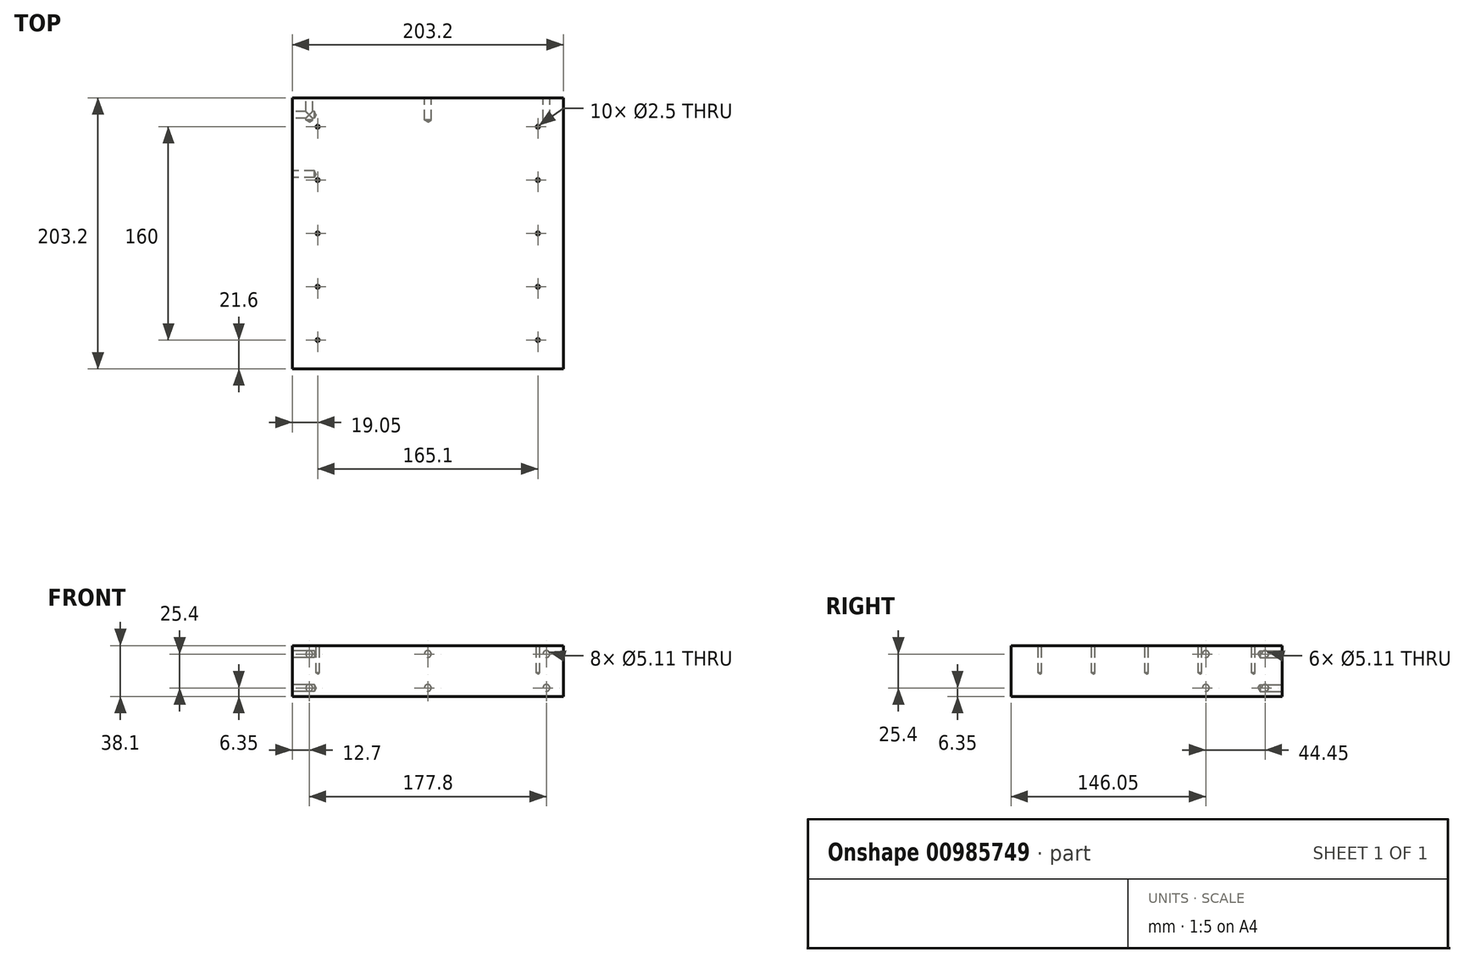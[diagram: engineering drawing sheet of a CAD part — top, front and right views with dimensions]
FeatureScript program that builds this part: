
annotation { "Feature Type Name" : "Feature", "Feature Type Description" : "" }
export const myFeature = defineFeature(function(context is Context, id is Id, definition is map)
    precondition{}
    {
        {
            var Q0;
            Q0=qCreatedBy(makeId("Top.planeOp"),FACE);
            var sketch = newSketch(context, id + "F0", { "sketchPlane" : qUnion([Q0])});
            skLineSegment(sketch, "E0.bottom", {"start": v(-101.6, 0) * mm, "end": v(101.6, 0) * mm});
            skLineSegment(sketch, "E0.top", {"start": v(-101.6, 203.2) * mm, "end": v(101.6, 203.2) * mm});
            skLineSegment(sketch, "E0.left", {"start": v(-101.6, 0) * mm, "end": v(-101.6, 203.2) * mm});
            skLineSegment(sketch, "E0.right", {"start": v(101.6, 0) * mm, "end": v(101.6, 203.2) * mm});
            skSolve(sketch);
        }
        {
            var Q0;
            Q0 = qSketchRegion(id + "F0", true);
            extrude(context, id + "F1", {"entities" : qUnion([Q0]), "depth" : 38.1 * mm, "offsetDistance" : 25.4 * mm});
        }
        {
            var Q0;
            {var subQ0=sQuery(id+"F0.wireOp",EDGE,"E0.bottom");var subQ2=sQuery(id+"F0.wireOp",EDGE,"E0.left");Q0=makeQuery(id+"FGkV8nF4XjDxECF_1.boolean.opBoolean","SPLIT",FACE,{"disambiguationData":[TD([makeQuery(id+"F1.opExtrude","SWEPT_FACE",FACE,{"disambiguationData":[OSD([subQ0])]})])],"derivedFrom":makeQuery(id+"F1.opExtrude","SWEPT_FACE",FACE,{"disambiguationData":[OSD([subQ2])]})});}
            var sketch = newSketch(context, id + "F2", { "sketchPlane" : qUnion([Q0])});
            skLineSegment(sketch, "E1", {"start": v(-190.5, 31.75) * mm, "end": v(-190.5, 6.35) * mm, "construction": true});
            skLineSegment(sketch, "E2", {"start": v(-190.5, 6.35) * mm, "end": v(-146.05, 6.35) * mm, "construction": true});
            skLineSegment(sketch, "E3", {"start": v(-146.05, 6.35) * mm, "end": v(-146.05, 31.75) * mm, "construction": true});
            skLineSegment(sketch, "E4", {"start": v(-146.05, 31.75) * mm, "end": v(-190.5, 31.75) * mm, "construction": true});
            skLineSegment(sketch, "E5", {"start": v(-203.2, 19.05) * mm, "end": v(-190.5, 19.05) * mm, "construction": true});
            skPoint(sketch, "E6", {"position": v(-190.5, 31.75) * mm});
            skPoint(sketch, "E7", {"position": v(-190.5, 6.35) * mm});
            skPoint(sketch, "E8", {"position": v(-146.05, 6.35) * mm});
            skPoint(sketch, "E9", {"position": v(-146.05, 31.75) * mm});
            skSolve(sketch);
        }
        {
            var Q0;
            Q0=sQuery(id+"F2.wireOp",VERTEX,"E6");
            var Q1;
            Q1=sQuery(id+"F2.wireOp",VERTEX,"E7");
            var Q2;
            Q2=sQuery(id+"F2.wireOp",VERTEX,"E8");
            var Q3;
            Q3=sQuery(id+"F2.wireOp",VERTEX,"E9");
            var Q4;
            Q4=makeQuery(id+"F1.opExtrude","SWEPT_BODY",BODY,{"disambiguationData":[OSD([sQuery(id+"F0.wireOp",EDGE,"E0.bottom"),sQuery(id+"F0.wireOp",EDGE,"E0.top"),sQuery(id+"F0.wireOp",EDGE,"E0.left"),sQuery(id+"F0.wireOp",EDGE,"E0.right")])]});
            hole(context, id + "F3", {"style" : HoleStyle.SIMPLE, "endStyle" : HoleEndStyle.BLIND, "standardTappedOrClearance" : lookupTablePath({ "standard" : "ANSI", "engagement" : "75%", "pitch" : "20 tpi", "size" : "1/4", "type" : "Tapped" }), "standardBlindInLast" : lookupTablePath({ "standard" : "ANSI", "fit" : "Free", "engagement" : "75%", "pitch" : "20 tpi", "size" : "1/4", "type" : "Clearance & tapped" }), "holeDiameter" : 5.1 * mm, "majorDiameter" : 6.35 * mm, "showTappedDepth" : true, "holeDepth" : 16.51 * mm, "isTappedThrough" : true, "tappedDepth" : 12.7 * mm, "tapClearance" : 3, "startFromSketch" : true, "locations" : qUnion([Q0, Q1, Q2, Q3]), "scope" : qUnion([Q4])});
        }
        {
            var Q0;
            Q0=makeQuery(id+"F1.opExtrude","SWEPT_FACE",FACE,{"disambiguationData":[OSD([sQuery(id+"F0.wireOp",EDGE,"E0.top")])]});
            var sketch = newSketch(context, id + "F4", { "sketchPlane" : qUnion([Q0])});
            skLineSegment(sketch, "E10", {"start": v(-88.9, 6.35) * mm, "end": v(-88.9, 31.75) * mm, "construction": true});
            skLineSegment(sketch, "E11", {"start": v(-88.9, 31.75) * mm, "end": v(88.9, 31.75) * mm, "construction": true});
            skLineSegment(sketch, "E12", {"start": v(88.9, 31.75) * mm, "end": v(88.9, 6.35) * mm, "construction": true});
            skLineSegment(sketch, "E13", {"start": v(88.9, 6.35) * mm, "end": v(-88.9, 6.35) * mm, "construction": true});
            skLineSegment(sketch, "E14", {"start": v(0, 31.75) * mm, "end": v(0, 38.1) * mm, "construction": true});
            skLineSegment(sketch, "E15", {"start": v(-88.9, 19.05) * mm, "end": v(-101.6, 19.05) * mm, "construction": true});
            skPoint(sketch, "E16", {"position": v(-88.9, 31.75) * mm});
            skPoint(sketch, "E17", {"position": v(88.9, 31.75) * mm});
            skPoint(sketch, "E18", {"position": v(88.9, 6.35) * mm});
            skPoint(sketch, "E19", {"position": v(-88.9, 6.35) * mm});
            skPoint(sketch, "E20", {"position": v(0, 31.75) * mm});
            skPoint(sketch, "E21", {"position": v(0, 6.35) * mm});
            skSolve(sketch);
        }
        {
            var Q0;
            Q0=sQuery(id+"F4.wireOp",VERTEX,"E16");
            var Q1;
            Q1=sQuery(id+"F4.wireOp",VERTEX,"E19");
            var Q2;
            Q2=sQuery(id+"F4.wireOp",VERTEX,"E17");
            var Q3;
            Q3=sQuery(id+"F4.wireOp",VERTEX,"E18");
            var Q4;
            Q4=sQuery(id+"F4.wireOp",VERTEX,"E20");
            var Q5;
            Q5=sQuery(id+"F4.wireOp",VERTEX,"E21");
            var Q6;
            Q6=makeQuery(id+"F1.opExtrude","SWEPT_BODY",BODY,{"disambiguationData":[OSD([sQuery(id+"F0.wireOp",EDGE,"E0.bottom"),sQuery(id+"F0.wireOp",EDGE,"E0.top"),sQuery(id+"F0.wireOp",EDGE,"E0.left"),sQuery(id+"F0.wireOp",EDGE,"E0.right")])]});
            hole(context, id + "F5", {"style" : HoleStyle.SIMPLE, "endStyle" : HoleEndStyle.BLIND, "standardTappedOrClearance" : lookupTablePath({ "standard" : "ANSI", "engagement" : "75%", "pitch" : "20 tpi", "size" : "1/4", "type" : "Tapped" }), "standardBlindInLast" : lookupTablePath({ "standard" : "ANSI", "fit" : "Free", "engagement" : "75%", "pitch" : "20 tpi", "size" : "1/4", "type" : "Clearance & tapped" }), "holeDiameter" : 5.1 * mm, "majorDiameter" : 6.35 * mm, "showTappedDepth" : true, "holeDepth" : 16.51 * mm, "isTappedThrough" : true, "tappedDepth" : 12.7 * mm, "tapClearance" : 3, "startFromSketch" : true, "locations" : qUnion([Q0, Q1, Q2, Q3, Q4, Q5]), "scope" : qUnion([Q6])});
        }
        {
            var Q0;
            Q0=makeQuery(id+"F1.opExtrude","CAP_FACE",FACE,{"disambiguationData":[OSD([sQuery(id+"F0.wireOp",EDGE,"E0.bottom"),sQuery(id+"F0.wireOp",EDGE,"E0.top"),sQuery(id+"F0.wireOp",EDGE,"E0.left"),sQuery(id+"F0.wireOp",EDGE,"E0.right")])],"isStart":false});
            var sketch = newSketch(context, id + "F6", { "sketchPlane" : qUnion([Q0])});
            skLineSegment(sketch, "E22", {"start": v(-82.55, 21.6) * mm, "end": v(-82.55, 61.6) * mm, "construction": true});
            skLineSegment(sketch, "E23", {"start": v(-82.55, 61.6) * mm, "end": v(-82.55, 101.6) * mm, "construction": true});
            skLineSegment(sketch, "E24", {"start": v(-82.55, 101.6) * mm, "end": v(-82.55, 141.6) * mm, "construction": true});
            skLineSegment(sketch, "E25", {"start": v(-82.55, 141.6) * mm, "end": v(-82.55, 181.6) * mm, "construction": true});
            skLineSegment(sketch, "E26", {"start": v(-82.55, 181.6) * mm, "end": v(82.55, 181.6) * mm, "construction": true});
            skLineSegment(sketch, "E27", {"start": v(82.55, 181.6) * mm, "end": v(82.55, 141.6) * mm, "construction": true});
            skLineSegment(sketch, "E28", {"start": v(82.55, 141.6) * mm, "end": v(-82.55, 141.6) * mm, "construction": true});
            skLineSegment(sketch, "E29", {"start": v(-82.55, 101.6) * mm, "end": v(82.55, 101.6) * mm, "construction": true});
            skLineSegment(sketch, "E30", {"start": v(82.55, 141.6) * mm, "end": v(82.55, 101.6) * mm, "construction": true});
            skLineSegment(sketch, "E31", {"start": v(82.55, 101.6) * mm, "end": v(82.55, 61.6) * mm, "construction": true});
            skLineSegment(sketch, "E32", {"start": v(82.55, 61.6) * mm, "end": v(82.55, 21.6) * mm, "construction": true});
            skLineSegment(sketch, "E33", {"start": v(82.55, 21.6) * mm, "end": v(-82.55, 21.6) * mm, "construction": true});
            skLineSegment(sketch, "E34", {"start": v(-82.55, 61.6) * mm, "end": v(82.55, 61.6) * mm, "construction": true});
            skLineSegment(sketch, "E35", {"start": v(0, 21.6) * mm, "end": v(0, 0) * mm, "construction": true});
            skLineSegment(sketch, "E36", {"start": v(0, 181.6) * mm, "end": v(0, 203.2) * mm, "construction": true});
            skPoint(sketch, "E37", {"position": v(-82.55, 181.6) * mm});
            skPoint(sketch, "E38", {"position": v(-82.55, 141.6) * mm});
            skPoint(sketch, "E39", {"position": v(-82.55, 101.6) * mm});
            skPoint(sketch, "E40", {"position": v(-82.55, 61.6) * mm});
            skPoint(sketch, "E41", {"position": v(-82.55, 21.6) * mm});
            skPoint(sketch, "E42", {"position": v(82.55, 21.6) * mm});
            skPoint(sketch, "E43", {"position": v(82.55, 61.6) * mm});
            skPoint(sketch, "E44", {"position": v(82.55, 101.6) * mm});
            skPoint(sketch, "E45", {"position": v(82.55, 141.6) * mm});
            skPoint(sketch, "E46", {"position": v(82.55, 181.6) * mm});
            skSolve(sketch);
        }
        {
            var Q0;
            Q0=sQuery(id+"F6.wireOp",VERTEX,"E37");
            var Q1;
            Q1=sQuery(id+"F6.wireOp",VERTEX,"E38");
            var Q2;
            Q2=sQuery(id+"F6.wireOp",VERTEX,"E39");
            var Q3;
            Q3=sQuery(id+"F6.wireOp",VERTEX,"E40");
            var Q4;
            Q4=sQuery(id+"F6.wireOp",VERTEX,"E41");
            var Q5;
            Q5=sQuery(id+"F6.wireOp",VERTEX,"E42");
            var Q6;
            Q6=sQuery(id+"F6.wireOp",VERTEX,"E43");
            var Q7;
            Q7=sQuery(id+"F6.wireOp",VERTEX,"E44");
            var Q8;
            Q8=sQuery(id+"F6.wireOp",VERTEX,"E45");
            var Q9;
            Q9=sQuery(id+"F6.wireOp",VERTEX,"E46");
            var Q10;
            Q10=makeQuery(id+"F1.opExtrude","SWEPT_BODY",BODY,{"disambiguationData":[OSD([sQuery(id+"F0.wireOp",EDGE,"E0.bottom"),sQuery(id+"F0.wireOp",EDGE,"E0.top"),sQuery(id+"F0.wireOp",EDGE,"E0.left"),sQuery(id+"F0.wireOp",EDGE,"E0.right")])]});
            hole(context, id + "F7", {"style" : HoleStyle.SIMPLE, "endStyle" : HoleEndStyle.BLIND, "standardTappedOrClearance" : lookupTablePath({ "standard" : "ISO", "engagement" : "75%", "pitch" : "0.5 mm", "size" : "M3", "type" : "Tapped" }), "standardBlindInLast" : lookupTablePath({ "standard" : "ISO", "fit" : "Normal", "engagement" : "75%", "pitch" : "0.5 mm", "size" : "M3", "type" : "Clearance & tapped" }), "holeDiameter" : 2.5 * mm, "majorDiameter" : 3 * mm, "showTappedDepth" : true, "holeDepth" : 20.55 * mm, "isTappedThrough" : true, "tappedDepth" : 19.05 * mm, "tapClearance" : 3, "startFromSketch" : true, "locations" : qUnion([Q0, Q1, Q2, Q3, Q4, Q5, Q6, Q7, Q8, Q9]), "scope" : qUnion([Q10])});
        }
    });
